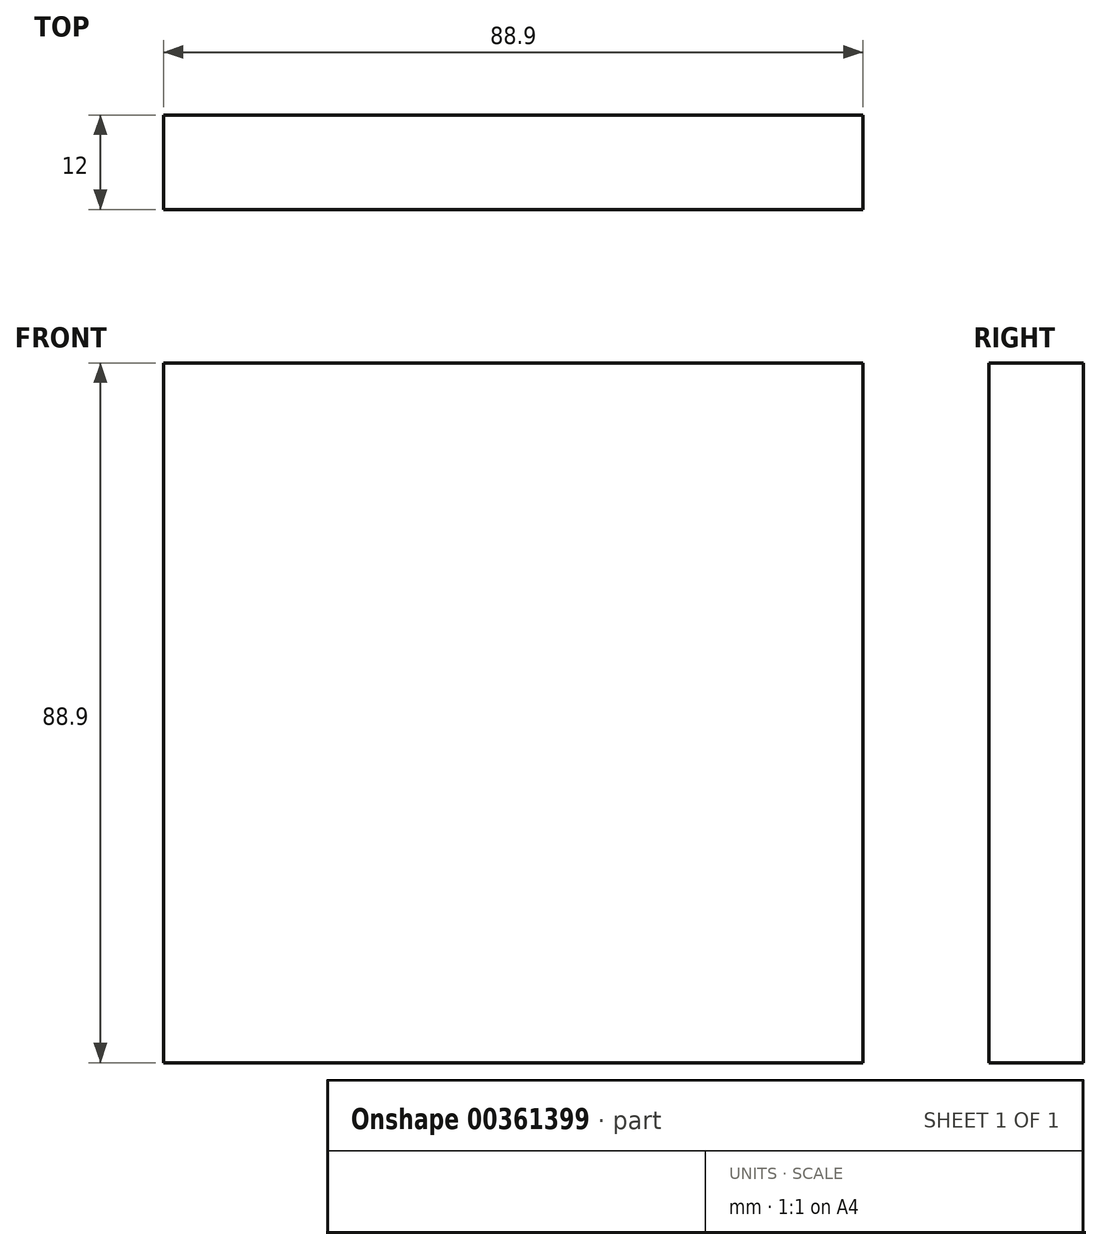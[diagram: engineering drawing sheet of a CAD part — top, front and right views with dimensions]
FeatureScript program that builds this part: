
annotation { "Feature Type Name" : "Feature", "Feature Type Description" : "" }
export const myFeature = defineFeature(function(context is Context, id is Id, definition is map)
    precondition{}
    {
        {
            var Q0;
            Q0=qCreatedBy(makeId("Front.planeOp"),FACE);
            var sketch = newSketch(context, id + "F0", { "sketchPlane" : qUnion([Q0])});
            skLineSegment(sketch, "E0.bottom", {"start": v(0, 0) * mm, "end": v(88.9, 0) * mm});
            skLineSegment(sketch, "E0.top", {"start": v(0, 88.9) * mm, "end": v(88.9, 88.9) * mm});
            skLineSegment(sketch, "E0.left", {"start": v(0, 0) * mm, "end": v(0, 88.9) * mm});
            skLineSegment(sketch, "E0.right", {"start": v(88.9, 0) * mm, "end": v(88.9, 88.9) * mm});
            skSolve(sketch);
        }
        {
            assignVariable(context, id + "F1", {"name" : "cut_length", "anyValue" : 12});
        }
        {
            var Q0;
            Q0=makeQuery(id+"F0.imprint","IMPRINT",FACE,{"disambiguationData":[TD([[makeQuery(id+"F0.imprint","IMPRINT",EDGE,{"derivedFrom":sQuery(id+"F0.wireOp",EDGE,"E0.bottom")}),1.0]])]});
            extrude(context, id + "F2", {"entities" : qUnion([Q0]), "oppositeDirection" : true, "depth" : (getVariable(context, 'cut_length')) * mm});
        }
    });
